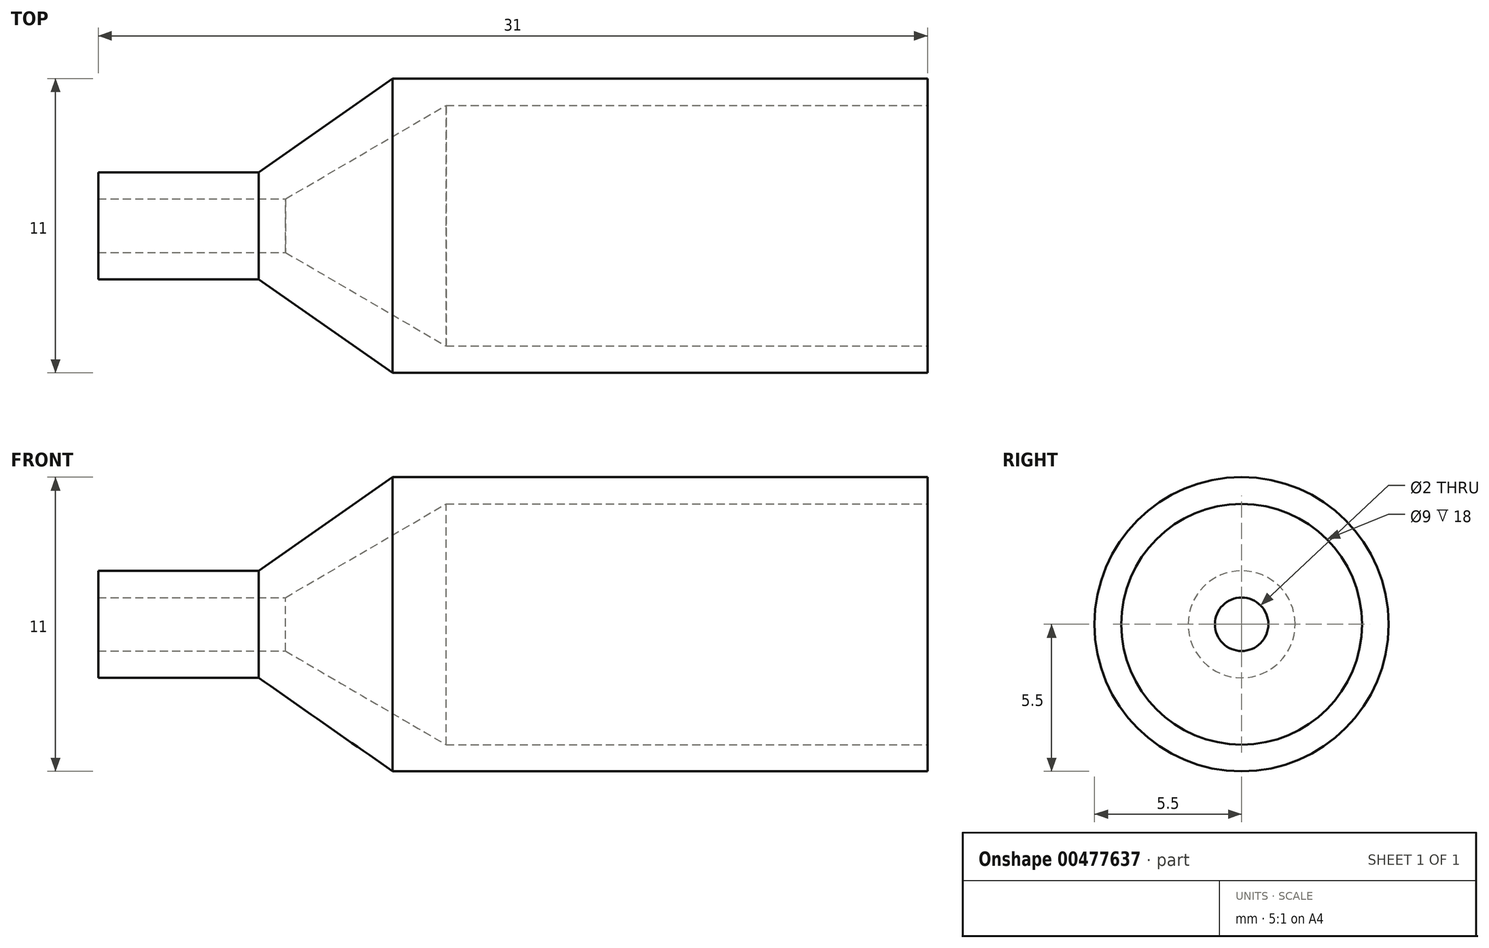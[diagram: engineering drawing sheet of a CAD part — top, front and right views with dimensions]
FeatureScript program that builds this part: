
annotation { "Feature Type Name" : "Feature", "Feature Type Description" : "" }
export const myFeature = defineFeature(function(context is Context, id is Id, definition is map)
    precondition{}
    {
        {
            var Q0;
            Q0=qCreatedBy(makeId("Front.planeOp"),FACE);
            var sketch = newSketch(context, id + "F0", { "sketchPlane" : qUnion([Q0])});
            skLineSegment(sketch, "E0", {"start": v(-50.5, 0) * mm, "end": v(53.5, 0) * mm, "construction": true});
            skLineSegment(sketch, "E1", {"start": v(-21.5, 1) * mm, "end": v(-14.5, 1) * mm});
            skLineSegment(sketch, "E2", {"start": v(-14.5, 1) * mm, "end": v(-8.5, 4.5) * mm});
            skLineSegment(sketch, "E3", {"start": v(-8.5, 4.5) * mm, "end": v(9.5, 4.5) * mm});
            skLineSegment(sketch, "E4", {"start": v(9.5, 5.5) * mm, "end": v(9.5, 4.5) * mm});
            skLineSegment(sketch, "E5", {"start": v(9.5, 5.5) * mm, "end": v(-10.5, 5.5) * mm});
            skLineSegment(sketch, "E6", {"start": v(-10.5, 5.5) * mm, "end": v(-15.5, 2) * mm});
            skLineSegment(sketch, "E7", {"start": v(-15.5, 2) * mm, "end": v(-21.5, 2) * mm});
            skLineSegment(sketch, "E8", {"start": v(-21.5, 1) * mm, "end": v(-21.5, 2) * mm});
            skSolve(sketch);
        }
        {
            var Q0;
            Q0=makeQuery(id+"F0.imprint","IMPRINT",FACE,{"disambiguationData":[TD([[makeQuery(id+"F0.imprint","IMPRINT",EDGE,{"derivedFrom":sQuery(id+"F0.wireOp",EDGE,"E1")}),1.0]])]});
            var Q1;
            Q1=sQuery(id+"F0.wireOp",EDGE,"E0");
            revolve(context, id + "F1", {"entities" : qUnion([Q0]), "axis" : qUnion([Q1]), "revolveType" : RevolveType.FULL, "oppositeDirection" : true});
        }
    });
